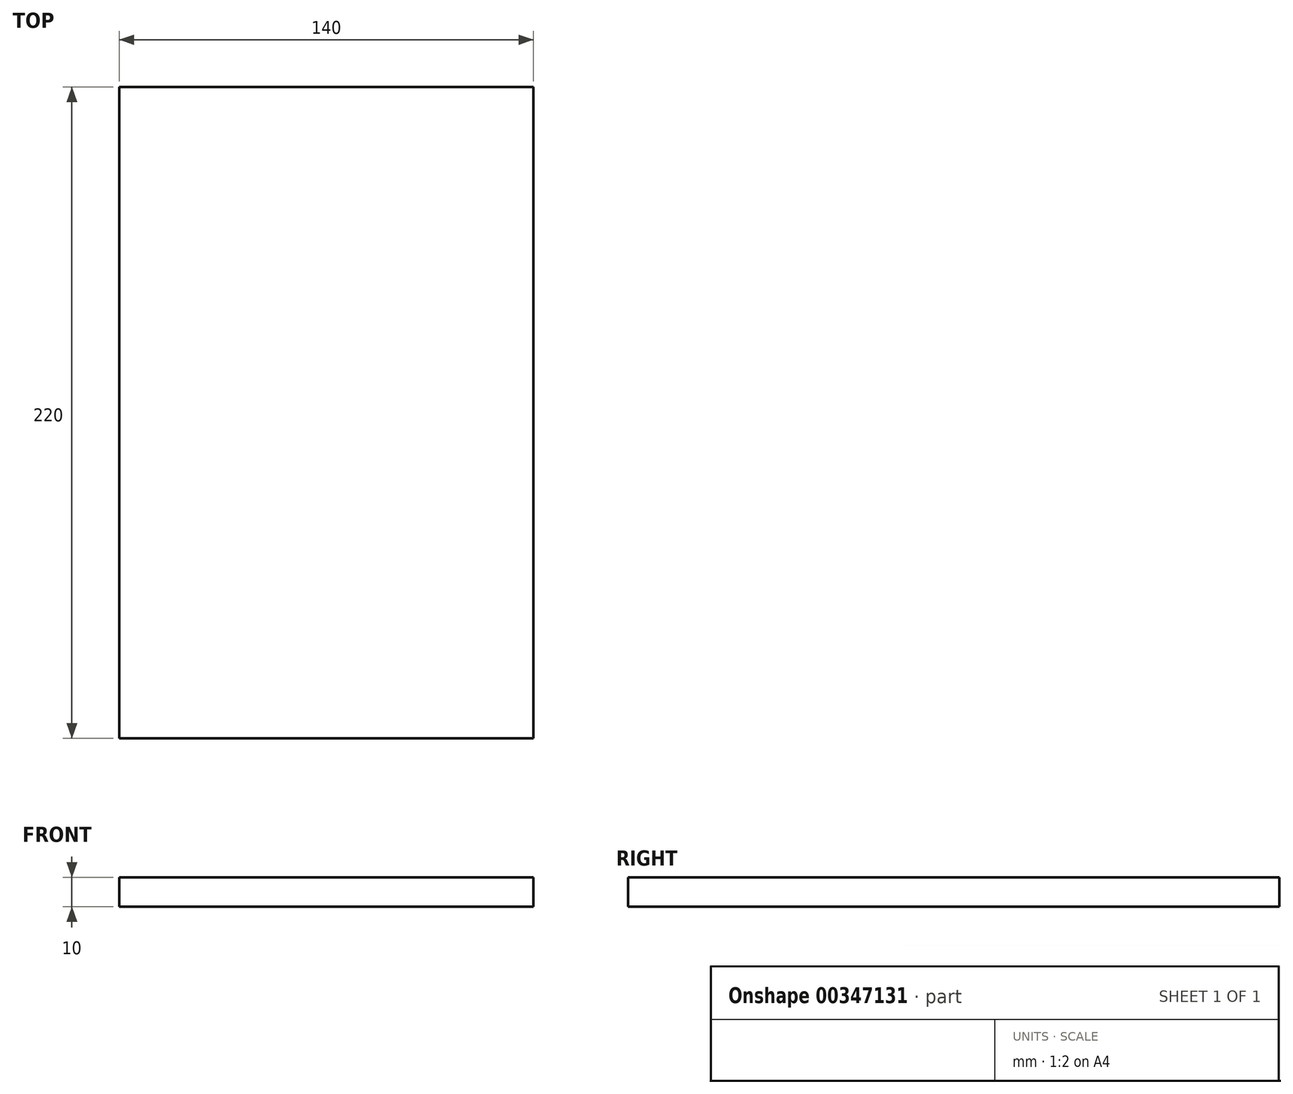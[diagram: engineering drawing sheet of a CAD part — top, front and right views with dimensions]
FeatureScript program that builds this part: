
annotation { "Feature Type Name" : "Feature", "Feature Type Description" : "" }
export const myFeature = defineFeature(function(context is Context, id is Id, definition is map)
    precondition{}
    {
        {
            var Q0;
            Q0=qCreatedBy(makeId("Top.planeOp"),FACE);
            var sketch = newSketch(context, id + "F0", { "sketchPlane" : qUnion([Q0])});
            skLineSegment(sketch, "E0.bottom", {"start": v(-70, 110) * mm, "end": v(70, 110) * mm});
            skLineSegment(sketch, "E0.top", {"start": v(-70, -110) * mm, "end": v(70, -110) * mm});
            skLineSegment(sketch, "E0.left", {"start": v(-70, 110) * mm, "end": v(-70, -110) * mm});
            skLineSegment(sketch, "E0.right", {"start": v(70, 110) * mm, "end": v(70, -110) * mm});
            skPoint(sketch, "E0.middle", {"position": v(0, 0) * mm});
            skPoint(sketch, "E1.visualSharp", {"position": v(-70, 110) * mm});
            skLineSegment(sketch, "E1.filletArc", {"start": v(-70, 110) * mm, "end": v(-70, 110) * mm});
            skPoint(sketch, "E2.visualSharp", {"position": v(70, 110) * mm});
            skLineSegment(sketch, "E2.filletArc", {"start": v(70, 110) * mm, "end": v(70, 110) * mm});
            skPoint(sketch, "E3.visualSharp", {"position": v(70, -110) * mm});
            skLineSegment(sketch, "E3.filletArc", {"start": v(70, -110) * mm, "end": v(70, -110) * mm});
            skPoint(sketch, "E4.visualSharp", {"position": v(-70, -110) * mm});
            skLineSegment(sketch, "E4.filletArc", {"start": v(-70, -110) * mm, "end": v(-70, -110) * mm});
            skSolve(sketch);
        }
        {
            var Q0;
            Q0=qSketchRegion(id+"F0",true);
            extrude(context, id + "F1", {"entities" : qUnion([Q0]), "depth" : 10 * mm});
        }
    });
